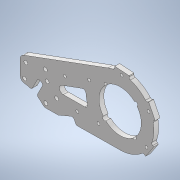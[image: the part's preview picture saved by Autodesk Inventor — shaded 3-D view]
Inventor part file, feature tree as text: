
AUTODESK INVENTOR PART (.ipt)
format: ipt  version: 2020 (Build 240168000, 168)  size: 504,832 bytes
history: native  units: mm
features: reference x24, extrude x8, sketch x8, other x7, fillet x5, projected_geometry x3, thicken_offset x1, hole x1, shell x1
ambient origin geometry x8: Origin, YZ Plane, XZ Plane, XY Plane, X Axis, Y Axis, Z Axis, Center Point
bodies: Solid1 (feature_tree)
feature tree (58):
  extrude  "Extrusion1"  Depth=9.0mm
  extrude  "Extrusion2"  Depth=12.0mm
  fillet  "Fillet1"  Radius=12.0mm
  thicken_offset  "Thicken1"
  extrude  "Extrusion3"  Depth=5.0mm
  extrude  "Extrusion5"  Depth=5.0mm
  fillet  "Fillet2"  Radius=5.0mm
  hole  "Hole1"  [1 undecoded]
  fillet  "Fillet3"  Radius=2.0mm
  extrude  "Extrusion7"  Depth=5.0mm
  fillet  "Fillet4"  Radius=5.0mm
  extrude  "Extrusion8"  Depth=3.0mm
  extrude  "Extrusion12"  Depth=2.0mm
  extrude  "Extrusion13"  Depth=2.0mm
  fillet  "Fillet5"  Radius=8.0mm
  sketch  "Sketch1"  dims[d0=70.0mm d1=9.0mm]
  reference  "Reference1"
  reference  "Reference2"
  reference  "Reference3"
  reference  "Reference4"
  reference  "Reference5"
  reference  "Reference6"
  reference  "Reference7"
  reference  "Reference8"
  reference  "Reference9"
  reference  "Reference10"
  reference  "Reference11"
  reference  "Reference12"
  sketch  "Sketch2"  dims[d2=9.0mm d3=12.0mm d4=12.0mm]
  reference  "Reference13"
  reference  "Reference14"
  sketch  "Sketch3"  dims[d5=5.0mm d6=0.0mm d7=9.0mm]
  reference  "Reference15"
  reference  "Reference16"
  projected_geometry  "Projected Loop1"
  sketch  "Sketch5"  dims[d8=6.0mm d9=19.0mm d10=5.0mm d11=0.0mm]
  reference  "Reference18"
  reference  "Reference19"
  reference  "Reference20"
  sketch  "Sketch6"  dims[d12=2.0mm d13=2.0mm d14=2.0mm]
  reference  "Reference21"
  reference  "Reference22"
  reference  "Reference23"
  reference  "Reference24"
  projected_geometry  "Projected Loop3"
  sketch  "Sketch9"  dims[d15=13.0mm d16=17.0mm d17=5.0mm d18=0.0mm]
  projected_geometry  "Projected Loop4"
  sketch  "Sketch13"  dims[d21=5.0mm d22=0.0mm d23=3.0mm]
  reference  "Reference28"
  sketch  "Sketch14"  dims[d24=3.0mm d25=6.0mm d26=4.0mm d27=2.0mm d28=90.0deg d29=8.0mm d30=20.594885mm d31=2.0mm d39=70.0mm d40=8.0mm d41=8.0mm d43=4.0mm d44=10.0mm d45=0.0mm d46=3.0mm d47=4.0mm d48=10.0mm d49=4.0mm d50=10.0mm d51=0.0mm d64=44.0mm d65=4.0mm d66=40.0mm d68=360.0deg d70=10.0mm d71=0.0mm d72=8.0mm d73=15.0mm d74=8.0mm d75=15.0mm d76=8.0mm d77=15.0mm d78=5.0mm d79=0.0mm d80=2.0mm]
  parser-record x1  (decoder bookkeeping rows leaked as tree rows — omitted from the tree; the rows remain in map.json)
  other  "reducer_leg.iam"
  other  "bearing_35_44_5:2"
  shell  "shell_2:4"  Thickness=8.0mm
  other  "motor_h_4:1"
  other  "motor_h_1:1"
  other  "end_holder_3:1"
  other  "end_holder_4:1"
note: 1 required parameter value undecoded (feature->parameter linkage not recoverable at this tier; creation-order binding heuristic only, values carry confidence <= 0.55)
note: 1 file-system path scrubbed to <path> (originals preserved in map.json)
